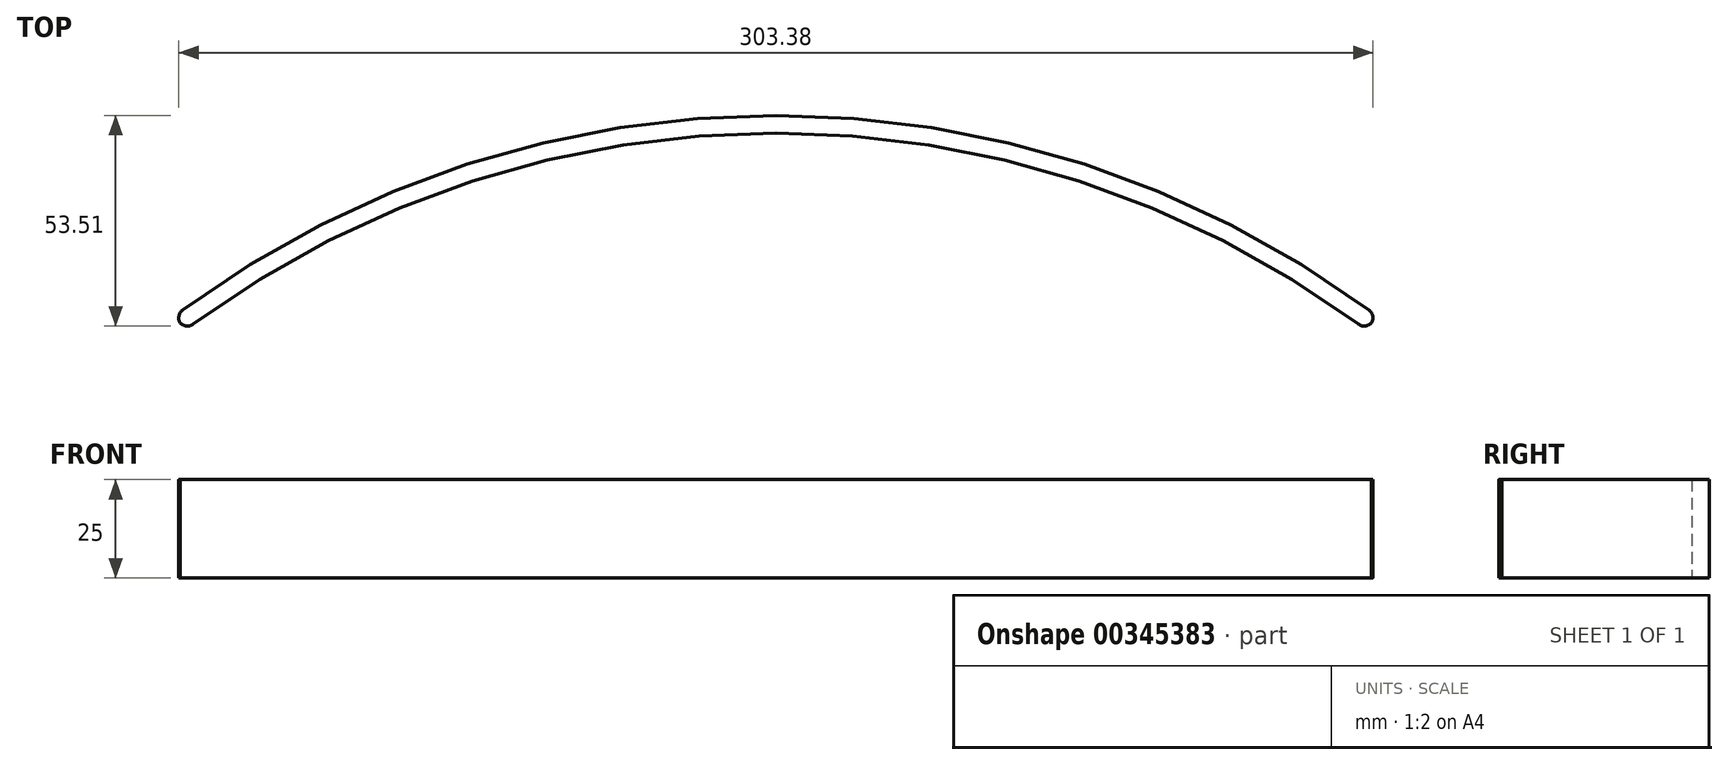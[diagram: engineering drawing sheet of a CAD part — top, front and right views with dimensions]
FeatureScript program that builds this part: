
annotation { "Feature Type Name" : "Feature", "Feature Type Description" : "" }
export const myFeature = defineFeature(function(context is Context, id is Id, definition is map)
    precondition{}
    {
        {
            var Q0;
            Q0=qCreatedBy(makeId("Top.planeOp"),FACE);
            var sketch = newSketch(context, id + "F0", { "sketchPlane" : qUnion([Q0])});
            skLineSegment(sketch, "E0", {"start": v(0, 0) * mm, "end": v(150, 0) * mm, "construction": true});
            skLineSegment(sketch, "E1", {"start": v(0, 0) * mm, "end": v(0, 50) * mm, "construction": true});
            skLineSegment(sketch, "E2.MirrorCS", {"start": v(0, 0) * mm, "end": v(-150, 0) * mm, "construction": true});
            skArc(sketch, "E3", {"start": v(150, 0) * mm, "mid": v(0, 50) * mm, "end": v(-150, 0) * mm});
            skArc(sketch, "E4.0", {"start": v(152.7, 3.6) * mm, "mid": v(0, 54.5) * mm, "end": v(-152.7, 3.6) * mm});
            skLineSegment(sketch, "E5", {"start": v(-152.7, 3.6) * mm, "end": v(-150, 0) * mm});
            skLineSegment(sketch, "E6", {"start": v(150, 0) * mm, "end": v(152.7, 3.6) * mm});
            skSolve(sketch);
        }
        {
            var Q0;
            Q0=makeQuery(id+"F0.imprint","IMPRINT",FACE,{"disambiguationData":[TD([[makeQuery(id+"F0.imprint","IMPRINT",EDGE,{"derivedFrom":sQuery(id+"F0.wireOp",EDGE,"E3")}),-1.0]])]});
            extrude(context, id + "F1", {"entities" : qUnion([Q0]), "depth" : 25 * mm});
        }
        {
            var Q0;
            Q0=makeQuery(id+"F1.opExtrude","SWEPT_EDGE",EDGE,{"disambiguationData":[OSD([sQuery(id+"F0.wireOp",EDGE,"E4.0"),sQuery(id+"F0.wireOp",EDGE,"E5")])]});
            var Q1;
            Q1=makeQuery(id+"F1.opExtrude","SWEPT_EDGE",EDGE,{"disambiguationData":[OSD([sQuery(id+"F0.wireOp",EDGE,"E3"),sQuery(id+"F0.wireOp",EDGE,"E5")])]});
            var Q2;
            Q2=makeQuery(id+"F1.opExtrude","SWEPT_EDGE",EDGE,{"disambiguationData":[OSD([sQuery(id+"F0.wireOp",EDGE,"E4.0"),sQuery(id+"F0.wireOp",EDGE,"E6")])]});
            var Q3;
            Q3=makeQuery(id+"F1.opExtrude","SWEPT_EDGE",EDGE,{"disambiguationData":[OSD([sQuery(id+"F0.wireOp",EDGE,"E3"),sQuery(id+"F0.wireOp",EDGE,"E6")])]});
            fillet(context, id + "F2", {"entities" : qUnion([Q0, Q1, Q2, Q3]), "radius" : 2.5 * mm, "tangentPropagation" : true, "allowEdgeOverflow" : false});
        }
    });
